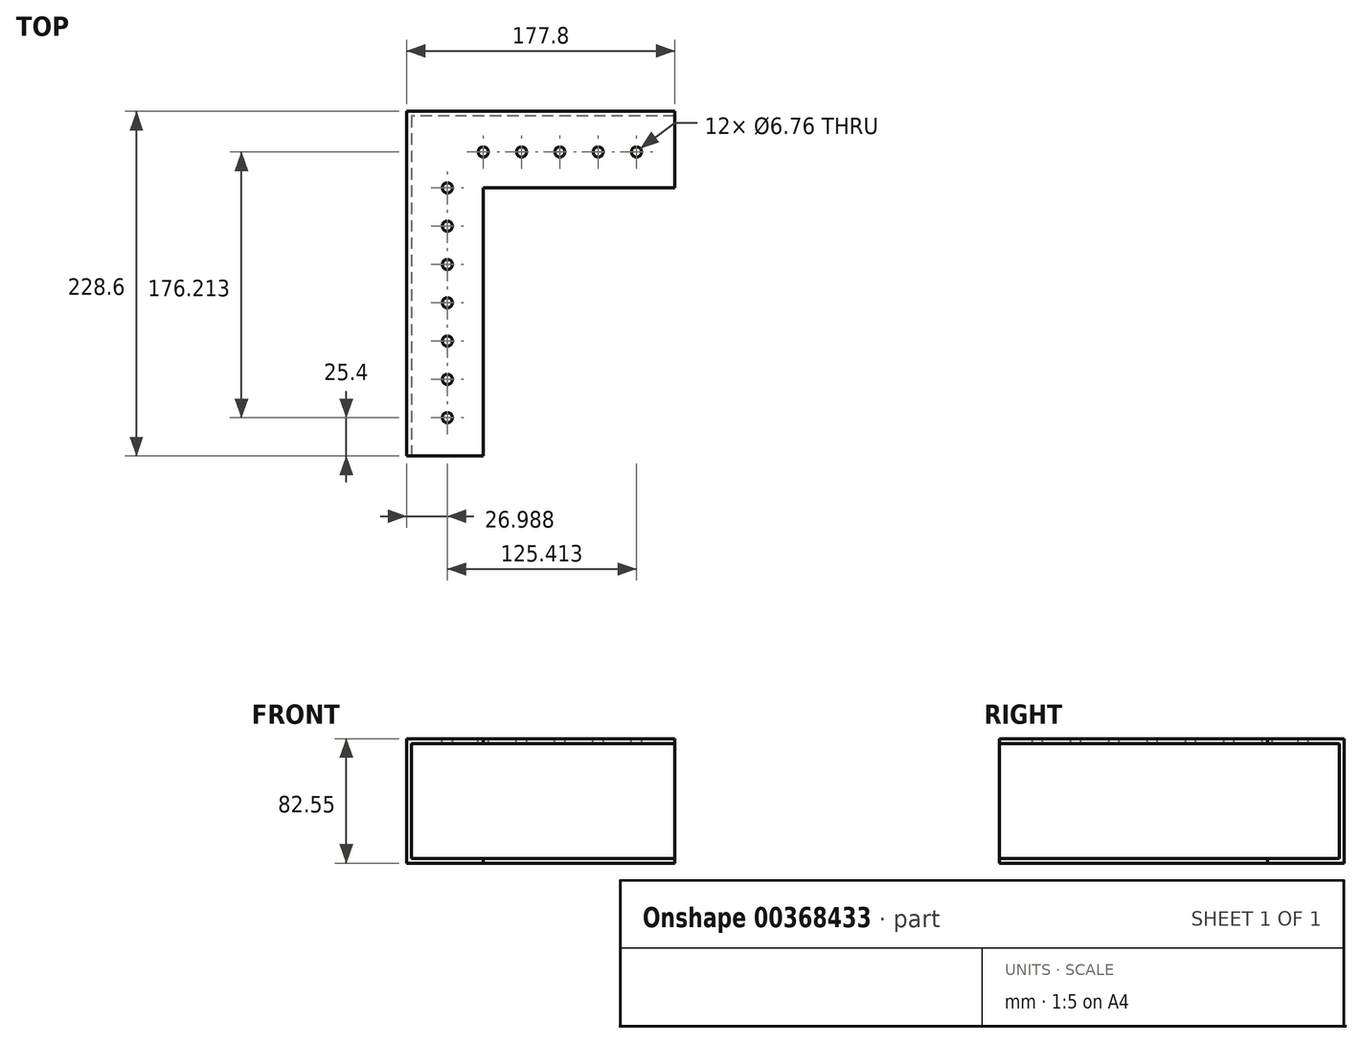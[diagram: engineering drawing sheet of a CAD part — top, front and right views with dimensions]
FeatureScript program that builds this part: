
annotation { "Feature Type Name" : "Feature", "Feature Type Description" : "" }
export const myFeature = defineFeature(function(context is Context, id is Id, definition is map)
    precondition{}
    {
        {
            var Q0;
            Q0=qCreatedBy(makeId("Top.planeOp"),FACE);
            var sketch = newSketch(context, id + "F0", { "sketchPlane" : qUnion([Q0])});
            skLineSegment(sketch, "E0.bottom", {"start": v(0, 0) * mm, "end": v(50.8, 0) * mm});
            skLineSegment(sketch, "E0.top", {"start": v(0, 177.8) * mm, "end": v(50.8, 177.8) * mm});
            skLineSegment(sketch, "E0.left", {"start": v(0, 0) * mm, "end": v(0, 177.8) * mm});
            skLineSegment(sketch, "E0.right", {"start": v(50.8, 0) * mm, "end": v(50.8, 177.8) * mm});
            skLineSegment(sketch, "E1.bottom", {"start": v(0, 228.6) * mm, "end": v(177.8, 228.6) * mm});
            skLineSegment(sketch, "E1.top", {"start": v(0, 177.8) * mm, "end": v(177.8, 177.8) * mm});
            skLineSegment(sketch, "E1.left", {"start": v(0, 228.6) * mm, "end": v(0, 177.8) * mm});
            skLineSegment(sketch, "E1.right", {"start": v(177.8, 228.6) * mm, "end": v(177.8, 177.8) * mm});
            skSolve(sketch);
        }
        {
            var Q0;
            Q0=makeQuery(id+"F0.imprint","IMPRINT",FACE,{"disambiguationData":[TD([[makeQuery(id+"F0.imprint","IMPRINT",EDGE,{"derivedFrom":sQuery(id+"F0.wireOp",EDGE,"E1.bottom")}),-1.0]])]});
            var Q1;
            Q1=makeQuery(id+"F0.imprint","IMPRINT",FACE,{"disambiguationData":[TD([[makeQuery(id+"F0.imprint","IMPRINT",EDGE,{"derivedFrom":sQuery(id+"F0.wireOp",EDGE,"E0.bottom")}),1.0]])]});
            extrude(context, id + "F1", {"entities" : qUnion([Q0, Q1]), "depth" : 3.17 * mm});
        }
        {
            var Q0;
            Q0=makeQuery(id+"F1.opExtrude","CAP_FACE",FACE,{"disambiguationData":[OSD([sQuery(id+"F0.wireOp",EDGE,"E0.bottom"),sQuery(id+"F0.wireOp",EDGE,"E0.left"),sQuery(id+"F0.wireOp",EDGE,"E0.right"),sQuery(id+"F0.wireOp",EDGE,"E1.bottom"),sQuery(id+"F0.wireOp",EDGE,"E1.top"),sQuery(id+"F0.wireOp",EDGE,"E1.left"),sQuery(id+"F0.wireOp",EDGE,"E1.right")])],"isStart":false});
            var sketch = newSketch(context, id + "F2", { "sketchPlane" : qUnion([Q0])});
            skLineSegment(sketch, "E2.0.0", {"start": v(177.8, 228.6) * mm, "end": v(0, 228.6) * mm, "construction": true});
            skLineSegment(sketch, "E2.0.1", {"start": v(0, 228.6) * mm, "end": v(0, 0) * mm, "construction": true});
            skLineSegment(sketch, "E2.0.2", {"start": v(0, 0) * mm, "end": v(50.8, 0) * mm, "construction": true});
            skLineSegment(sketch, "E2.0.3", {"start": v(50.8, 0) * mm, "end": v(50.8, 177.8) * mm, "construction": true});
            skLineSegment(sketch, "E2.0.4", {"start": v(50.8, 177.8) * mm, "end": v(177.8, 177.8) * mm, "construction": true});
            skLineSegment(sketch, "E2.0.5", {"start": v(177.8, 177.8) * mm, "end": v(177.8, 228.6) * mm, "construction": true});
            skLineSegment(sketch, "E3.0", {"start": v(3.18, 225.43) * mm, "end": v(3.18, 0) * mm});
            skLineSegment(sketch, "E4.0", {"start": v(177.8, 225.43) * mm, "end": v(3.17, 225.43) * mm});
            skLineSegment(sketch, "E5", {"start": v(177.8, 225.43) * mm, "end": v(177.8, 228.6) * mm});
            skLineSegment(sketch, "E6", {"start": v(177.8, 228.6) * mm, "end": v(0, 228.6) * mm});
            skLineSegment(sketch, "E7", {"start": v(0, 228.6) * mm, "end": v(0, 0) * mm});
            skLineSegment(sketch, "E8", {"start": v(0, 0) * mm, "end": v(3.18, 0) * mm});
            skSolve(sketch);
        }
        {
            var Q0;
            Q0=makeQuery(id+"F2.imprint","IMPRINT",FACE,{"disambiguationData":[TD([[makeQuery(id+"F2.imprint","IMPRINT",EDGE,{"derivedFrom":sQuery(id+"F2.wireOp",EDGE,"E3.0")}),-1.0]])]});
            extrude(context, id + "F3", {"entities" : qUnion([Q0]), "operationType" : NewBodyOperationType.ADD, "depth" : 76.2 * mm});
        }
        {
            var Q0;
            Q0=makeQuery(id+"F3.opExtrude","CAP_FACE",FACE,{"disambiguationData":[OSD([sQuery(id+"F2.wireOp",EDGE,"E3.0"),sQuery(id+"F2.wireOp",EDGE,"E4.0"),sQuery(id+"F2.wireOp",EDGE,"E5"),sQuery(id+"F2.wireOp",EDGE,"E6"),sQuery(id+"F2.wireOp",EDGE,"E7"),sQuery(id+"F2.wireOp",EDGE,"E8")])],"isStart":false});
            var sketch = newSketch(context, id + "F4", { "sketchPlane" : qUnion([Q0])});
            skLineSegment(sketch, "E9.0.0", {"start": v(0, 228.6) * mm, "end": v(177.8, 228.6) * mm});
            skLineSegment(sketch, "E9.0.1", {"start": v(177.8, 228.6) * mm, "end": v(177.8, 177.8) * mm});
            skLineSegment(sketch, "E9.0.2", {"start": v(177.8, 177.8) * mm, "end": v(50.8, 177.8) * mm});
            skLineSegment(sketch, "E9.0.3", {"start": v(50.8, 177.8) * mm, "end": v(50.8, 0) * mm});
            skLineSegment(sketch, "E9.0.4", {"start": v(50.8, 0) * mm, "end": v(0, 0) * mm});
            skLineSegment(sketch, "E9.0.5", {"start": v(0, 0) * mm, "end": v(0, 228.6) * mm});
            skSolve(sketch);
        }
        {
            var Q0;
            {var subQ4=sQuery(id+"F4.wireOp",EDGE,"E9.0.0");Q0=makeQuery(id+"F4.imprint","IMPRINT",FACE,{"disambiguationData":[TD([[makeQuery(id+"F4.imprint","IMPRINT",EDGE,{"derivedFrom":subQ4}),-1.0]])]});}
            var Q1;
            {var subQ3=sQuery(id+"F4.wireOp",EDGE,"E9.0.2");Q1=makeQuery(id+"F4.imprint","IMPRINT",FACE,{"disambiguationData":[TD([[makeQuery(id+"F4.imprint","IMPRINT",EDGE,{"derivedFrom":subQ3}),-1.0]])]});}
            extrude(context, id + "F5", {"entities" : qUnion([Q0, Q1]), "operationType" : NewBodyOperationType.ADD, "depth" : 3.17 * mm});
        }
        {
            var Q0;
            Q0=makeQuery(id+"F5.opExtrude","CAP_FACE",FACE,{"disambiguationData":[OSD([sQuery(id+"F4.wireOp",EDGE,"E9.0.0"),sQuery(id+"F4.wireOp",EDGE,"E9.0.1"),sQuery(id+"F4.wireOp",EDGE,"E9.0.2"),sQuery(id+"F4.wireOp",EDGE,"E9.0.3"),sQuery(id+"F4.wireOp",EDGE,"E9.0.4"),sQuery(id+"F4.wireOp",EDGE,"E9.0.5")])],"isStart":false});
            var sketch = newSketch(context, id + "F6", { "sketchPlane" : qUnion([Q0])});
            skLineSegment(sketch, "E10.0.0", {"start": v(50.8, 177.8) * mm, "end": v(177.8, 177.8) * mm, "construction": true});
            skLineSegment(sketch, "E10.0.1", {"start": v(177.8, 177.8) * mm, "end": v(177.8, 228.6) * mm, "construction": true});
            skLineSegment(sketch, "E10.0.2", {"start": v(177.8, 228.6) * mm, "end": v(0, 228.6) * mm, "construction": true});
            skLineSegment(sketch, "E10.0.3", {"start": v(0, 228.6) * mm, "end": v(0, 0) * mm, "construction": true});
            skLineSegment(sketch, "E10.0.4", {"start": v(0, 0) * mm, "end": v(50.8, 0) * mm, "construction": true});
            skLineSegment(sketch, "E10.0.5", {"start": v(50.8, 0) * mm, "end": v(50.8, 177.8) * mm, "construction": true});
            skLineSegment(sketch, "E11.0.0", {"start": v(177.8, 177.8) * mm, "end": v(177.8, 225.43) * mm, "construction": true});
            skLineSegment(sketch, "E11.0.1", {"start": v(177.8, 225.43) * mm, "end": v(3.17, 225.43) * mm, "construction": true});
            skLineSegment(sketch, "E11.0.2", {"start": v(3.18, 225.43) * mm, "end": v(3.18, 0) * mm, "construction": true});
            skLineSegment(sketch, "E11.0.3", {"start": v(3.18, 0) * mm, "end": v(50.8, 0) * mm, "construction": true});
            skLineSegment(sketch, "E12", {"start": v(26.99, 0) * mm, "end": v(26.99, 201.61) * mm, "construction": true});
            skLineSegment(sketch, "E13", {"start": v(177.8, 201.61) * mm, "end": v(26.99, 201.61) * mm, "construction": true});
            skPoint(sketch, "E14", {"position": v(26.99, 25.4) * mm});
            skPoint(sketch, "E15", {"position": v(152.4, 201.61) * mm});
            skPoint(sketch, "E16.0.1.0", {"position": v(26.99, 50.8) * mm});
            skPoint(sketch, "E16.0.2.0", {"position": v(26.99, 76.2) * mm});
            skPoint(sketch, "E16.0.3.0", {"position": v(26.99, 101.6) * mm});
            skPoint(sketch, "E16.0.4.0", {"position": v(26.99, 127) * mm});
            skPoint(sketch, "E16.0.5.0", {"position": v(26.99, 152.4) * mm});
            skPoint(sketch, "E16.0.6.0", {"position": v(26.99, 177.8) * mm});
            skLineSegment(sketch, "E16.direction1", {"start": v(26.99, 25.4) * mm, "end": v(52.39, 25.4) * mm, "construction": true});
            skLineSegment(sketch, "E16.direction2", {"start": v(26.99, 25.4) * mm, "end": v(26.99, 50.8) * mm, "construction": true});
            skPoint(sketch, "E17.1.0.0", {"position": v(127, 201.61) * mm});
            skPoint(sketch, "E17.2.0.0", {"position": v(101.6, 201.61) * mm});
            skPoint(sketch, "E17.3.0.0", {"position": v(76.2, 201.61) * mm});
            skPoint(sketch, "E17.4.0.0", {"position": v(50.8, 201.61) * mm});
            skLineSegment(sketch, "E17.direction1", {"start": v(152.4, 201.61) * mm, "end": v(127, 201.61) * mm, "construction": true});
            skSolve(sketch);
        }
        {
            var Q0;
            Q0=sQuery(id+"F6.wireOp",VERTEX,"E14");
            var Q1;
            Q1=sQuery(id+"F6.wireOp",VERTEX,"E16.0.1.0");
            var Q2;
            Q2=sQuery(id+"F6.wireOp",VERTEX,"E16.0.2.0");
            var Q3;
            Q3=sQuery(id+"F6.wireOp",VERTEX,"E16.0.3.0");
            var Q4;
            Q4=sQuery(id+"F6.wireOp",VERTEX,"E16.0.4.0");
            var Q5;
            Q5=sQuery(id+"F6.wireOp",VERTEX,"E16.0.5.0");
            var Q6;
            Q6=sQuery(id+"F6.wireOp",VERTEX,"E16.0.6.0");
            var Q7;
            Q7=sQuery(id+"F6.wireOp",VERTEX,"E17.4.0.0");
            var Q8;
            Q8=sQuery(id+"F6.wireOp",VERTEX,"E17.3.0.0");
            var Q9;
            Q9=sQuery(id+"F6.wireOp",VERTEX,"E17.2.0.0");
            var Q10;
            Q10=sQuery(id+"F6.wireOp",VERTEX,"E17.1.0.0");
            var Q11;
            Q11=sQuery(id+"F6.wireOp",VERTEX,"E15");
            var Q12;
            Q12=makeQuery(id+"F1.opExtrude","SWEPT_BODY",BODY,{"disambiguationData":[OSD([sQuery(id+"F0.wireOp",EDGE,"E0.bottom"),sQuery(id+"F0.wireOp",EDGE,"E0.left"),sQuery(id+"F0.wireOp",EDGE,"E0.right"),sQuery(id+"F0.wireOp",EDGE,"E1.bottom"),sQuery(id+"F0.wireOp",EDGE,"E1.top"),sQuery(id+"F0.wireOp",EDGE,"E1.left"),sQuery(id+"F0.wireOp",EDGE,"E1.right")])]});
            hole(context, id + "F7", {"style" : HoleStyle.SIMPLE, "endStyle" : HoleEndStyle.BLIND, "standardTappedOrClearance" : lookupTablePath({ "standard" : "ANSI", "fit" : "Normal (ASME)", "size" : "1/4", "type" : "Clearance" }), "standardBlindInLast" : lookupTablePath({ "fit" : "Free", "standard" : "ANSI", "size" : "1/4", "type" : "Clearance" }), "holeDiameter" : 6.76 * mm, "holeDepth" : 29.2 * mm, "isTappedThrough" : true, "tappedDepth" : 25.4 * mm, "tapClearance" : 3, "locations" : qUnion([Q0, Q1, Q2, Q3, Q4, Q5, Q6, Q7, Q8, Q9, Q10, Q11]), "scope" : qUnion([Q12])});
        }
    });
